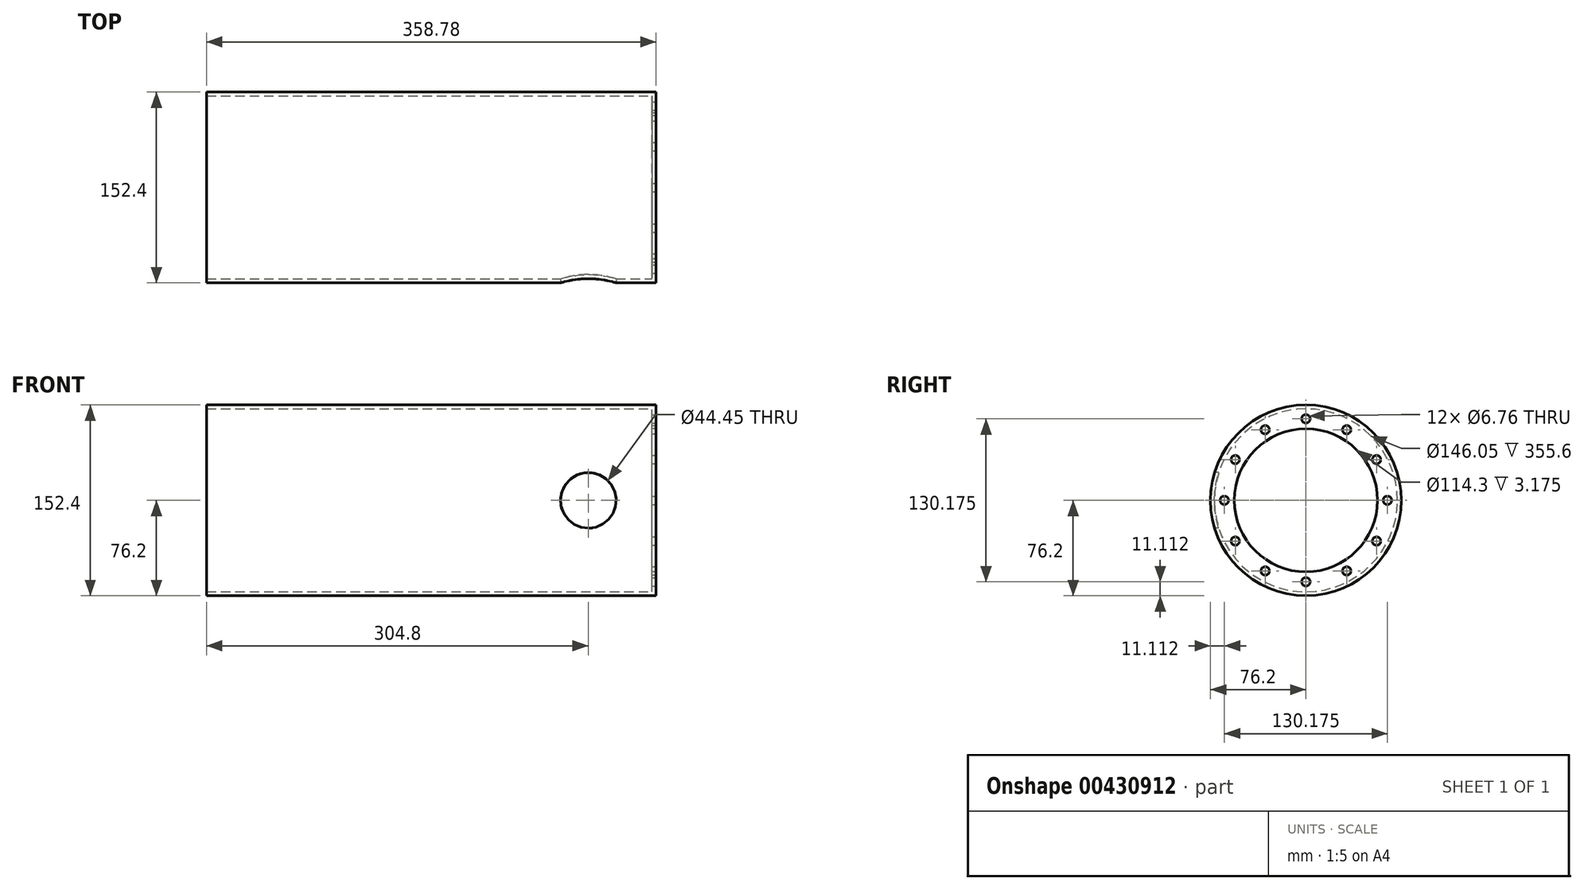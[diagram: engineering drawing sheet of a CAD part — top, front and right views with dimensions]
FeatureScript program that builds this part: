
annotation { "Feature Type Name" : "Feature", "Feature Type Description" : "" }
export const myFeature = defineFeature(function(context is Context, id is Id, definition is map)
    precondition{}
    {
        {
            var Q0;
            Q0=qCreatedBy(makeId("Right.planeOp"),FACE);
            var sketch = newSketch(context, id + "F0", { "sketchPlane" : qUnion([Q0])});
            skCircle(sketch, "E0", {"center": v(0, 0) * mm, "radius": 76.2 * mm});
            skCircle(sketch, "E1", {"center": v(0, 0) * mm, "radius": 73.03 * mm});
            skSolve(sketch);
        }
        {
            var Q0;
            Q0=makeQuery(id+"F0.imprint","IMPRINT",FACE,{"disambiguationData":[TD([[makeQuery(id+"F0.imprint","IMPRINT",EDGE,{"derivedFrom":sQuery(id+"F0.wireOp",EDGE,"E0")}),1.0]])]});
            extrude(context, id + "F1", {"entities" : qUnion([Q0]), "oppositeDirection" : true, "depth" : 355.6 * mm});
        }
        {
            var Q0;
            Q0=qCreatedBy(makeId("Right.planeOp"),FACE);
            var sketch = newSketch(context, id + "F2", { "sketchPlane" : qUnion([Q0])});
            skCircle(sketch, "E2", {"center": v(0, 0) * mm, "radius": 76.2 * mm});
            skCircle(sketch, "E3", {"center": v(0, 0) * mm, "radius": 57.15 * mm});
            skSolve(sketch);
        }
        {
            var Q0;
            Q0=makeQuery(id+"F2.imprint","IMPRINT",FACE,{"disambiguationData":[TD([[makeQuery(id+"F2.imprint","IMPRINT",EDGE,{"derivedFrom":sQuery(id+"F2.wireOp",EDGE,"E2")}),1.0]])]});
            extrude(context, id + "F3", {"entities" : qUnion([Q0]), "operationType" : NewBodyOperationType.ADD, "depth" : 3.17 * mm});
        }
        {
            var Q0;
            Q0=makeQuery(id+"F3.opExtrude","CAP_FACE",FACE,{"disambiguationData":[OSD([sQuery(id+"F2.wireOp",EDGE,"E2"),sQuery(id+"F2.wireOp",EDGE,"E3")])],"isStart":false});
            var sketch = newSketch(context, id + "F4", { "sketchPlane" : qUnion([Q0])});
            skCircle(sketch, "E4", {"center": v(0, 65.09) * mm, "radius": 3.38 * mm});
            skCircle(sketch, "E5.1.0", {"center": v(-32.54, 56.37) * mm, "radius": 3.38 * mm});
            skCircle(sketch, "E5.2.0", {"center": v(-56.37, 32.54) * mm, "radius": 3.38 * mm});
            skCircle(sketch, "E5.3.0", {"center": v(-65.09, 0) * mm, "radius": 3.38 * mm});
            skCircle(sketch, "E5.4.0", {"center": v(-56.37, -32.54) * mm, "radius": 3.38 * mm});
            skCircle(sketch, "E5.5.0", {"center": v(-32.54, -56.37) * mm, "radius": 3.38 * mm});
            skCircle(sketch, "E5.6.0", {"center": v(0, -65.09) * mm, "radius": 3.38 * mm});
            skCircle(sketch, "E5.7.0", {"center": v(32.54, -56.37) * mm, "radius": 3.38 * mm});
            skCircle(sketch, "E5.8.0", {"center": v(56.37, -32.54) * mm, "radius": 3.38 * mm});
            skCircle(sketch, "E5.9.0", {"center": v(65.09, 0) * mm, "radius": 3.38 * mm});
            skCircle(sketch, "E5.10.0", {"center": v(56.37, 32.54) * mm, "radius": 3.38 * mm});
            skCircle(sketch, "E5.11.0", {"center": v(32.54, 56.37) * mm, "radius": 3.38 * mm});
            skPoint(sketch, "E5.center", {"position": v(0, 0) * mm});
            skSolve(sketch);
        }
        {
            var Q0;
            Q0=makeQuery(id+"F4.imprint","IMPRINT",FACE,{"disambiguationData":[TD([[makeQuery(id+"F4.imprint","IMPRINT",EDGE,{"derivedFrom":sQuery(id+"F4.wireOp",EDGE,"E4")}),1.0]])]});
            var Q1;
            Q1=makeQuery(id+"F4.imprint","IMPRINT",FACE,{"disambiguationData":[TD([[makeQuery(id+"F4.imprint","IMPRINT",EDGE,{"derivedFrom":sQuery(id+"F4.wireOp",EDGE,"E5.11.0")}),1.0]])]});
            var Q2;
            Q2=makeQuery(id+"F4.imprint","IMPRINT",FACE,{"disambiguationData":[TD([[makeQuery(id+"F4.imprint","IMPRINT",EDGE,{"derivedFrom":sQuery(id+"F4.wireOp",EDGE,"E5.10.0")}),1.0]])]});
            var Q3;
            Q3=makeQuery(id+"F4.imprint","IMPRINT",FACE,{"disambiguationData":[TD([[makeQuery(id+"F4.imprint","IMPRINT",EDGE,{"derivedFrom":sQuery(id+"F4.wireOp",EDGE,"E5.9.0")}),1.0]])]});
            var Q4;
            Q4=makeQuery(id+"F4.imprint","IMPRINT",FACE,{"disambiguationData":[TD([[makeQuery(id+"F4.imprint","IMPRINT",EDGE,{"derivedFrom":sQuery(id+"F4.wireOp",EDGE,"E5.8.0")}),1.0]])]});
            var Q5;
            Q5=makeQuery(id+"F4.imprint","IMPRINT",FACE,{"disambiguationData":[TD([[makeQuery(id+"F4.imprint","IMPRINT",EDGE,{"derivedFrom":sQuery(id+"F4.wireOp",EDGE,"E5.7.0")}),1.0]])]});
            var Q6;
            Q6=makeQuery(id+"F4.imprint","IMPRINT",FACE,{"disambiguationData":[TD([[makeQuery(id+"F4.imprint","IMPRINT",EDGE,{"derivedFrom":sQuery(id+"F4.wireOp",EDGE,"E5.6.0")}),1.0]])]});
            var Q7;
            Q7=makeQuery(id+"F4.imprint","IMPRINT",FACE,{"disambiguationData":[TD([[makeQuery(id+"F4.imprint","IMPRINT",EDGE,{"derivedFrom":sQuery(id+"F4.wireOp",EDGE,"E5.5.0")}),1.0]])]});
            var Q8;
            Q8=makeQuery(id+"F4.imprint","IMPRINT",FACE,{"disambiguationData":[TD([[makeQuery(id+"F4.imprint","IMPRINT",EDGE,{"derivedFrom":sQuery(id+"F4.wireOp",EDGE,"E5.4.0")}),1.0]])]});
            var Q9;
            Q9=makeQuery(id+"F4.imprint","IMPRINT",FACE,{"disambiguationData":[TD([[makeQuery(id+"F4.imprint","IMPRINT",EDGE,{"derivedFrom":sQuery(id+"F4.wireOp",EDGE,"E5.3.0")}),1.0]])]});
            var Q10;
            Q10=makeQuery(id+"F4.imprint","IMPRINT",FACE,{"disambiguationData":[TD([[makeQuery(id+"F4.imprint","IMPRINT",EDGE,{"derivedFrom":sQuery(id+"F4.wireOp",EDGE,"E5.2.0")}),1.0]])]});
            var Q11;
            Q11=makeQuery(id+"F4.imprint","IMPRINT",FACE,{"disambiguationData":[TD([[makeQuery(id+"F4.imprint","IMPRINT",EDGE,{"derivedFrom":sQuery(id+"F4.wireOp",EDGE,"E5.1.0")}),1.0]])]});
            extrude(context, id + "F5", {"entities" : qUnion([Q0, Q1, Q2, Q3, Q4, Q5, Q6, Q7, Q8, Q9, Q10, Q11]), "operationType" : NewBodyOperationType.REMOVE, "endBound" : BoundingType.THROUGH_ALL, "oppositeDirection" : true, "depth" : 25.4 * mm});
        }
        {
            var Q0;
            Q0=qCreatedBy(makeId("Front.planeOp"),FACE);
            cPlane(context, id + "F6", {"entities" : qUnion([Q0]), "cplaneType" : CPlaneType.OFFSET, "offset" : 76.2 * mm, "width" : 152.4 * mm, "height" : 152.4 * mm});
        }
        {
            var Q0;
            Q0=qCreatedBy(id+"F6.planeOp",FACE);
            var sketch = newSketch(context, id + "F7", { "sketchPlane" : qUnion([Q0])});
            skCircle(sketch, "E6", {"center": v(-50.8, 0) * mm, "radius": 22.23 * mm});
            skSolve(sketch);
        }
        {
            var Q0;
            Q0=makeQuery(id+"F7.imprint","IMPRINT",FACE,{"disambiguationData":[TD([[makeQuery(id+"F7.imprint","IMPRINT",EDGE,{"derivedFrom":sQuery(id+"F7.wireOp",EDGE,"E6")}),1.0]])]});
            var Q1;
            Q1=makeQuery(id+"F1.opExtrude","SWEPT_FACE",FACE,{"disambiguationData":[OSD([sQuery(id+"F0.wireOp",EDGE,"E1")])]});
            extrude(context, id + "F8", {"entities" : qUnion([Q0]), "operationType" : NewBodyOperationType.REMOVE, "endBound" : BoundingType.UP_TO_SURFACE, "oppositeDirection" : true, "endBoundEntityFace" : qUnion([Q1]), "depth" : 25.4 * mm});
        }
    });
